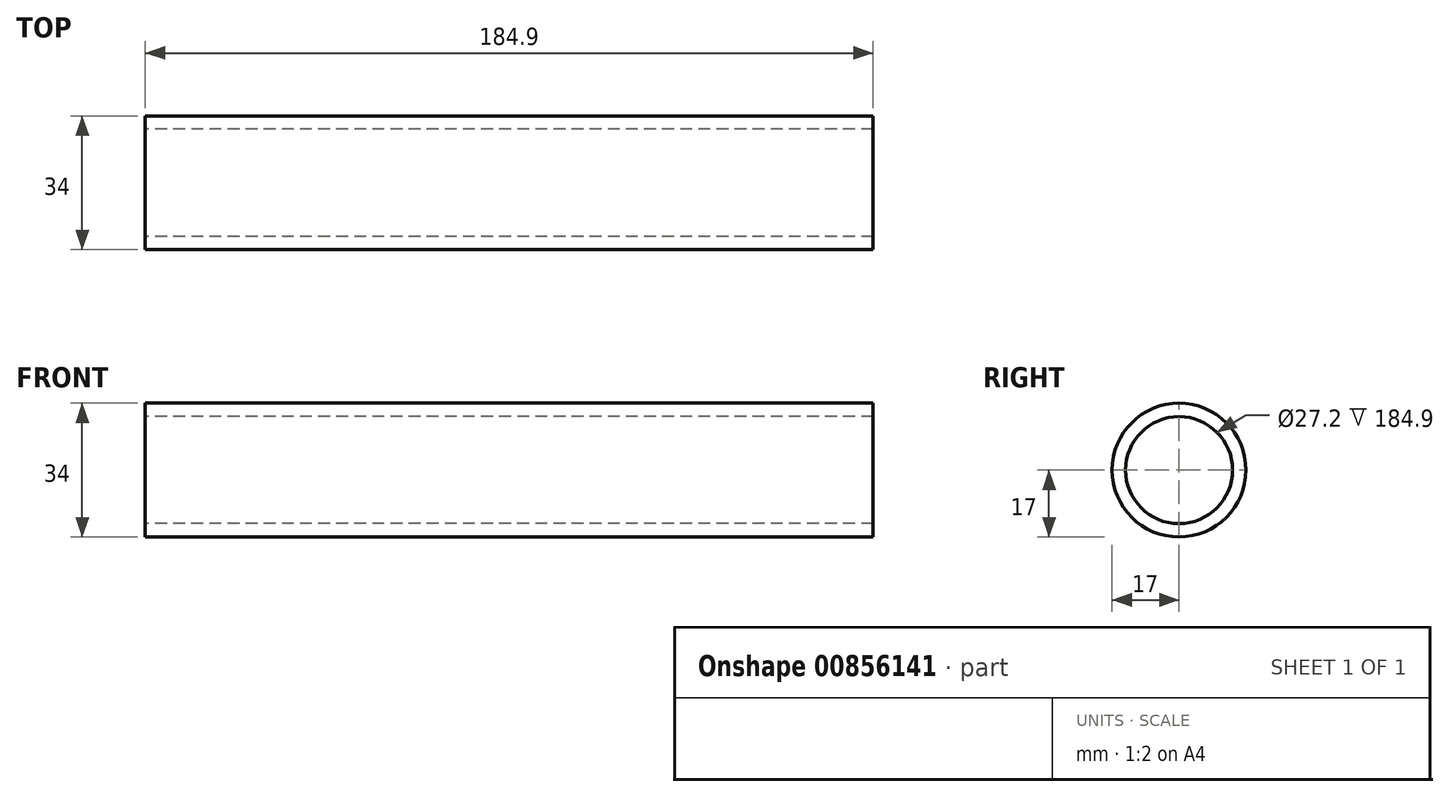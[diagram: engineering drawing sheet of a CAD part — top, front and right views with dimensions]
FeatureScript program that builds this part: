
annotation { "Feature Type Name" : "Feature", "Feature Type Description" : "" }
export const myFeature = defineFeature(function(context is Context, id is Id, definition is map)
    precondition{}
    {
        {
            var Q0;
            Q0=qCreatedBy(makeId("Right.planeOp"),FACE);
            var sketch = newSketch(context, id + "F0", { "sketchPlane" : qUnion([Q0])});
            skCircle(sketch, "E0", {"center": v(0, 0) * mm, "radius": 17 * mm});
            skSolve(sketch);
        }
        {
            var Q0;
            Q0=qCreatedBy(makeId("Front.planeOp"),FACE);
            var sketch = newSketch(context, id + "F1", { "sketchPlane" : qUnion([Q0])});
            skLineSegment(sketch, "E1", {"start": v(0, 0) * mm, "end": v(-184.9, 0) * mm});
            skSolve(sketch);
        }
        {
            var Q0;
            Q0=makeQuery(id+"F0.imprint","IMPRINT",FACE,{"disambiguationData":[TD([[makeQuery(id+"F0.imprint","IMPRINT",EDGE,{"derivedFrom":sQuery(id+"F0.wireOp",EDGE,"E0")}),1.0]])]});
            var Q1;
            Q1=sQuery(id+"F1.wireOp",EDGE,"E1");
            sweep(context, id + "F2", {"profiles" : qUnion([Q0]), "path" : qUnion([Q1])});
        }
        {
            var Q0;
            Q0=makeQuery(id+"F2.opSweep","CAP_FACE",FACE,{"disambiguationData":[OSD([sQuery(id+"F0.wireOp",EDGE,"E0"),sQuery(id+"F1.wireOp",VERTEX,"E1.end")])],"isStart":false});
            var Q1;
            Q1=makeQuery(id+"F2.opSweep","CAP_FACE",FACE,{"disambiguationData":[OSD([sQuery(id+"F0.wireOp",EDGE,"E0"),sQuery(id+"F1.wireOp",VERTEX,"E1.start")])],"isStart":true});
            shell(context, id + "F3", {"entities" : qUnion([Q0, Q1]), "thickness" : 3.4 * mm});
        }
    });
